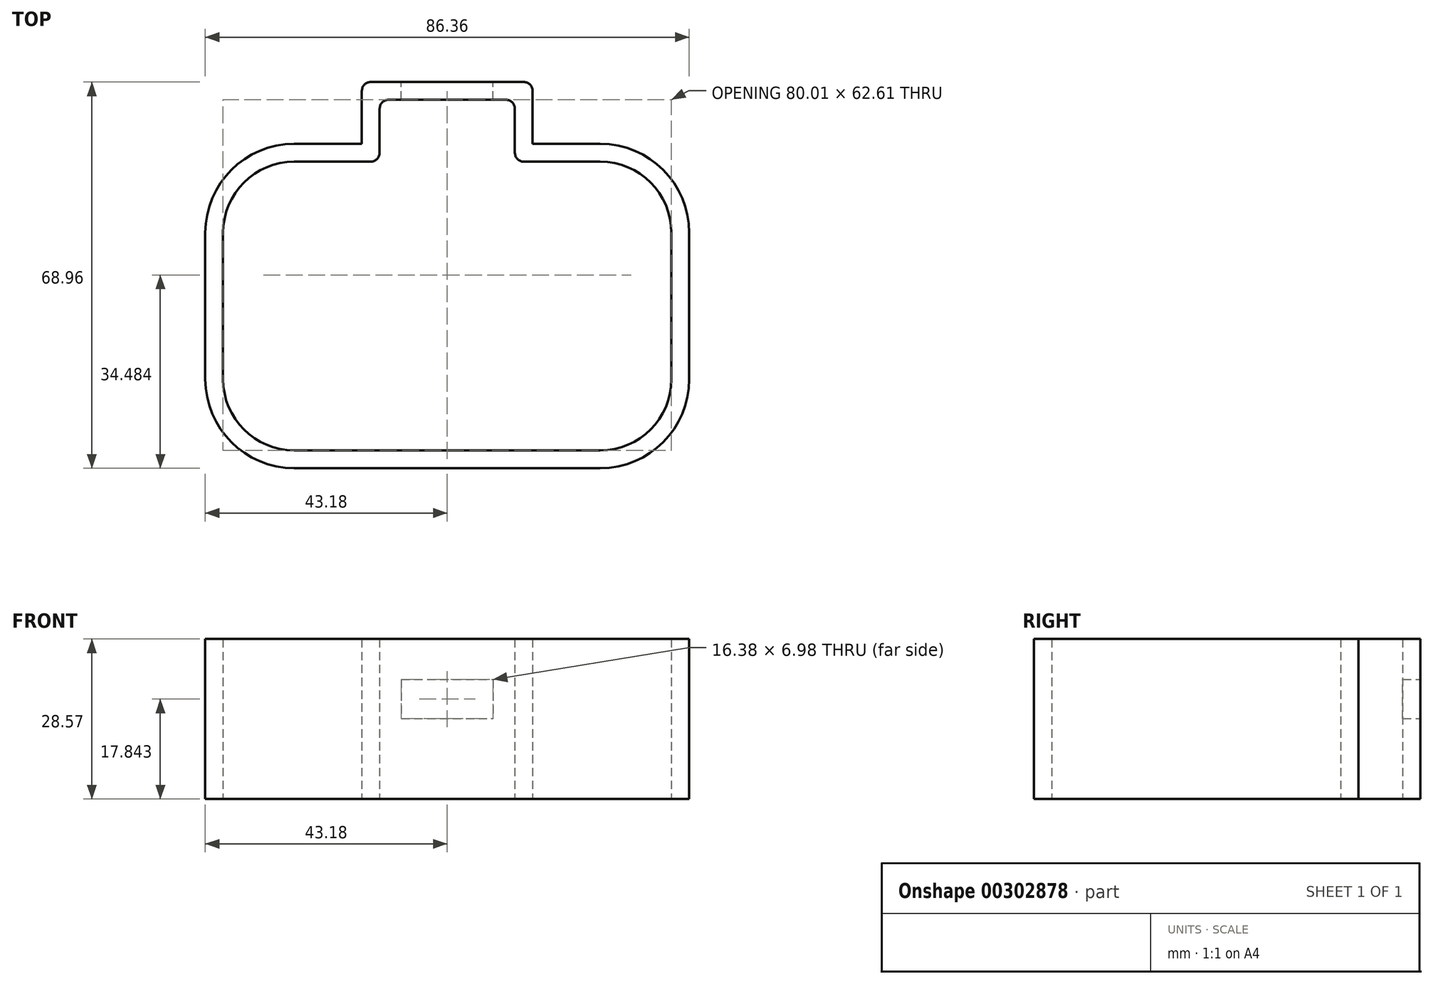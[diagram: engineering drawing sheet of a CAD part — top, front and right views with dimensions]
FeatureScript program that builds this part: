
annotation { "Feature Type Name" : "Feature", "Feature Type Description" : "" }
export const myFeature = defineFeature(function(context is Context, id is Id, definition is map)
    precondition{}
    {
        {
            var Q0;
            Q0=qCreatedBy(makeId("Top.planeOp"),FACE);
            var sketch = newSketch(context, id + "F0", { "sketchPlane" : qUnion([Q0])});
            skLineSegment(sketch, "E0.bottom", {"start": v(27.3, 25.78) * mm, "end": v(12.07, 25.78) * mm});
            skLineSegment(sketch, "E0.top", {"start": v(27.3, -25.78) * mm, "end": v(-27.3, -25.78) * mm});
            skLineSegment(sketch, "E0.left", {"start": v(40, 13.08) * mm, "end": v(40, -13.08) * mm});
            skLineSegment(sketch, "E0.right", {"start": v(-40, 13.08) * mm, "end": v(-40, -13.08) * mm});
            skPoint(sketch, "E0.middle", {"position": v(0, 0) * mm});
            skPoint(sketch, "E1.visualSharp", {"position": v(-40, -25.78) * mm});
            skArc(sketch, "E1.filletArc", {"start": v(-40, -13.08) * mm, "mid": v(-36.29, -22.06) * mm, "end": v(-27.3, -25.78) * mm});
            skPoint(sketch, "E2.visualSharp", {"position": v(-40, 25.78) * mm});
            skArc(sketch, "E2.filletArc", {"start": v(-27.3, 25.78) * mm, "mid": v(-36.29, 22.06) * mm, "end": v(-40, 13.08) * mm});
            skPoint(sketch, "E3.visualSharp", {"position": v(40, 25.78) * mm});
            skArc(sketch, "E3.filletArc", {"start": v(40, 13.08) * mm, "mid": v(36.29, 22.06) * mm, "end": v(27.3, 25.78) * mm});
            skPoint(sketch, "E4.visualSharp", {"position": v(40, -25.78) * mm});
            skArc(sketch, "E4.filletArc", {"start": v(27.3, -25.78) * mm, "mid": v(36.29, -22.06) * mm, "end": v(40, -13.08) * mm});
            skLineSegment(sketch, "E5", {"start": v(-12.06, 25.78) * mm, "end": v(-12.07, 36.83) * mm});
            skLineSegment(sketch, "E6", {"start": v(-12.07, 36.83) * mm, "end": v(12.06, 36.83) * mm});
            skLineSegment(sketch, "E7", {"start": v(12.06, 36.83) * mm, "end": v(12.07, 25.78) * mm});
            skLineSegment(sketch, "E8.trimOffspring", {"start": v(-12.06, 25.78) * mm, "end": v(-27.3, 25.78) * mm});
            skLineSegment(sketch, "E9.0", {"start": v(-15.24, 28.96) * mm, "end": v(-27.3, 28.96) * mm});
            skArc(sketch, "E9.1", {"start": v(27.3, -28.96) * mm, "mid": v(38.53, -24.3) * mm, "end": v(43.18, -13.08) * mm});
            skLineSegment(sketch, "E9.2", {"start": v(27.3, -28.96) * mm, "end": v(-27.3, -28.96) * mm});
            skArc(sketch, "E9.3", {"start": v(-43.18, -13.08) * mm, "mid": v(-38.53, -24.3) * mm, "end": v(-27.3, -28.96) * mm});
            skLineSegment(sketch, "E9.4", {"start": v(-43.18, 13.08) * mm, "end": v(-43.18, -13.08) * mm});
            skLineSegment(sketch, "E9.5", {"start": v(43.18, 13.08) * mm, "end": v(43.18, -13.08) * mm});
            skArc(sketch, "E9.6", {"start": v(-27.3, 28.96) * mm, "mid": v(-38.53, 24.3) * mm, "end": v(-43.18, 13.08) * mm});
            skArc(sketch, "E9.7", {"start": v(43.18, 13.08) * mm, "mid": v(38.53, 24.3) * mm, "end": v(27.3, 28.96) * mm});
            skLineSegment(sketch, "E9.8", {"start": v(27.3, 28.96) * mm, "end": v(15.24, 28.96) * mm});
            skLineSegment(sketch, "E9.9", {"start": v(15.24, 40) * mm, "end": v(15.24, 28.96) * mm});
            skLineSegment(sketch, "E9.10", {"start": v(-15.24, 40) * mm, "end": v(15.24, 40) * mm});
            skLineSegment(sketch, "E9.11", {"start": v(-15.24, 28.96) * mm, "end": v(-15.24, 40) * mm});
            skSolve(sketch);
        }
        {
            var Q0;
            Q0 = qSketchRegion(id + "F0", true);
            extrude(context, id + "F1", {"entities" : qUnion([Q0]), "depth" : 28.57 * mm});
        }
        {
            var Q0;
            Q0=makeQuery(id+"F1.opExtrude","SWEPT_FACE",FACE,{"disambiguationData":[OSD([sQuery(id+"F0.wireOp",EDGE,"E9.10")])]});
            var sketch = newSketch(context, id + "F2", { "sketchPlane" : qUnion([Q0])});
            skLineSegment(sketch, "E10.bottom", {"start": v(8.2, 21.34) * mm, "end": v(-8.2, 21.34) * mm});
            skLineSegment(sketch, "E10.top", {"start": v(8.2, 14.35) * mm, "end": v(-8.2, 14.35) * mm});
            skLineSegment(sketch, "E10.left", {"start": v(8.2, 21.34) * mm, "end": v(8.2, 14.35) * mm});
            skLineSegment(sketch, "E10.right", {"start": v(-8.2, 21.34) * mm, "end": v(-8.2, 14.35) * mm});
            skPoint(sketch, "E10.middle", {"position": v(0, 17.84) * mm});
            skSolve(sketch);
        }
        {
            var Q0;
            Q0 = qSketchRegion(id + "F2", true);
            extrude(context, id + "F3", {"entities" : qUnion([Q0]), "operationType" : NewBodyOperationType.REMOVE, "endBound" : BoundingType.UP_TO_NEXT, "oppositeDirection" : true, "depth" : 25.4 * mm});
        }
        {
            var Q0;
            Q0=makeQuery(id+"F1.opExtrude","SWEPT_EDGE",EDGE,{"disambiguationData":[OSD([sQuery(id+"F0.wireOp",EDGE,"E5"),sQuery(id+"F0.wireOp",EDGE,"E8.trimOffspring")])]});
            var Q1;
            Q1=makeQuery(id+"F1.opExtrude","SWEPT_EDGE",EDGE,{"disambiguationData":[OSD([sQuery(id+"F0.wireOp",EDGE,"E5"),sQuery(id+"F0.wireOp",EDGE,"E6")])]});
            var Q2;
            Q2=makeQuery(id+"F1.opExtrude","SWEPT_EDGE",EDGE,{"disambiguationData":[OSD([sQuery(id+"F0.wireOp",EDGE,"E0.bottom"),sQuery(id+"F0.wireOp",EDGE,"E7")])]});
            var Q3;
            Q3=makeQuery(id+"F1.opExtrude","SWEPT_EDGE",EDGE,{"disambiguationData":[OSD([sQuery(id+"F0.wireOp",EDGE,"E6"),sQuery(id+"F0.wireOp",EDGE,"E7")])]});
            var Q4;
            Q4=makeQuery(id+"F1.opExtrude","SWEPT_EDGE",EDGE,{"disambiguationData":[OSD([sQuery(id+"F0.wireOp",EDGE,"E9.9"),sQuery(id+"F0.wireOp",EDGE,"E9.10")])]});
            var Q5;
            Q5=makeQuery(id+"F1.opExtrude","SWEPT_EDGE",EDGE,{"disambiguationData":[OSD([sQuery(id+"F0.wireOp",EDGE,"E9.10"),sQuery(id+"F0.wireOp",EDGE,"E9.11")])]});
            fillet(context, id + "F4", {"entities" : qUnion([Q0, Q1, Q2, Q3, Q4, Q5]), "radius" : 1.59 * mm, "tangentPropagation" : true, "allowEdgeOverflow" : false});
        }
        {
            var Q0;
            Q0=makeQuery(id+"F1.opExtrude","SWEPT_BODY",BODY,{"disambiguationData":[OSD([sQuery(id+"F0.wireOp",EDGE,"E0.bottom"),sQuery(id+"F0.wireOp",EDGE,"E0.top"),sQuery(id+"F0.wireOp",EDGE,"E0.left"),sQuery(id+"F0.wireOp",EDGE,"E0.right"),sQuery(id+"F0.wireOp",EDGE,"E1.filletArc"),sQuery(id+"F0.wireOp",EDGE,"E2.filletArc"),sQuery(id+"F0.wireOp",EDGE,"E3.filletArc"),sQuery(id+"F0.wireOp",EDGE,"E4.filletArc"),sQuery(id+"F0.wireOp",EDGE,"E5"),sQuery(id+"F0.wireOp",EDGE,"E6"),sQuery(id+"F0.wireOp",EDGE,"E7"),sQuery(id+"F0.wireOp",EDGE,"E8.trimOffspring"),sQuery(id+"F0.wireOp",EDGE,"E9.0"),sQuery(id+"F0.wireOp",EDGE,"E9.1"),sQuery(id+"F0.wireOp",EDGE,"E9.2"),sQuery(id+"F0.wireOp",EDGE,"E9.3"),sQuery(id+"F0.wireOp",EDGE,"E9.4"),sQuery(id+"F0.wireOp",EDGE,"E9.5"),sQuery(id+"F0.wireOp",EDGE,"E9.6"),sQuery(id+"F0.wireOp",EDGE,"E9.7"),sQuery(id+"F0.wireOp",EDGE,"E9.8"),sQuery(id+"F0.wireOp",EDGE,"E9.9"),sQuery(id+"F0.wireOp",EDGE,"E9.10"),sQuery(id+"F0.wireOp",EDGE,"E9.11")])]});
            transform(context, id + "F5", {"entities" : qUnion([Q0]), "transformType" : TransformType.TRANSLATION_3D, "dx" : 0 * mm, "dy" : 0 * mm, "dz" : 0 * mm, "makeCopy" : true});
        }
        {
            var Q0;
            Q0=makeQuery(id+"F5.opPattern","COPY",BODY,{"derivedFrom":makeQuery(id+"F1.opExtrude","SWEPT_BODY",BODY,{"disambiguationData":[OSD([sQuery(id+"F0.wireOp",EDGE,"E0.bottom"),sQuery(id+"F0.wireOp",EDGE,"E0.top"),sQuery(id+"F0.wireOp",EDGE,"E0.left"),sQuery(id+"F0.wireOp",EDGE,"E0.right"),sQuery(id+"F0.wireOp",EDGE,"E1.filletArc"),sQuery(id+"F0.wireOp",EDGE,"E2.filletArc"),sQuery(id+"F0.wireOp",EDGE,"E3.filletArc"),sQuery(id+"F0.wireOp",EDGE,"E4.filletArc"),sQuery(id+"F0.wireOp",EDGE,"E5"),sQuery(id+"F0.wireOp",EDGE,"E6"),sQuery(id+"F0.wireOp",EDGE,"E7"),sQuery(id+"F0.wireOp",EDGE,"E8.trimOffspring"),sQuery(id+"F0.wireOp",EDGE,"E9.0"),sQuery(id+"F0.wireOp",EDGE,"E9.1"),sQuery(id+"F0.wireOp",EDGE,"E9.2"),sQuery(id+"F0.wireOp",EDGE,"E9.3"),sQuery(id+"F0.wireOp",EDGE,"E9.4"),sQuery(id+"F0.wireOp",EDGE,"E9.5"),sQuery(id+"F0.wireOp",EDGE,"E9.6"),sQuery(id+"F0.wireOp",EDGE,"E9.7"),sQuery(id+"F0.wireOp",EDGE,"E9.8"),sQuery(id+"F0.wireOp",EDGE,"E9.9"),sQuery(id+"F0.wireOp",EDGE,"E9.10"),sQuery(id+"F0.wireOp",EDGE,"E9.11")])]}),"instanceName":"1"});
            deleteBodies(context, id + "F6", {"entities" : qUnion([Q0])});
        }
    });
